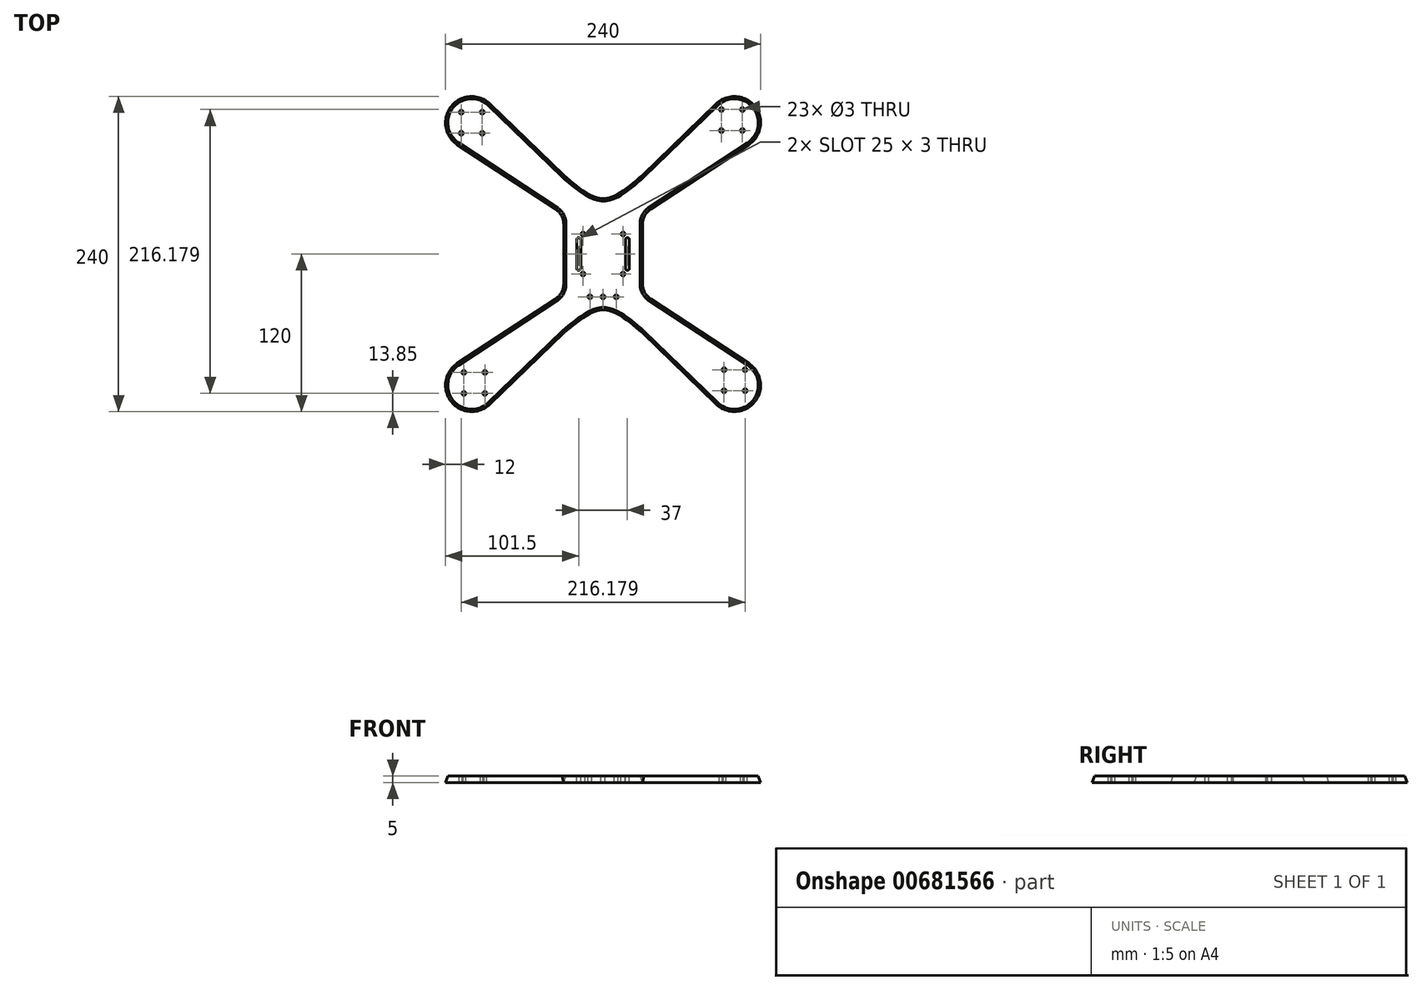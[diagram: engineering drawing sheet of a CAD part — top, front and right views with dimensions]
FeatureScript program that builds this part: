
annotation { "Feature Type Name" : "Feature", "Feature Type Description" : "" }
export const myFeature = defineFeature(function(context is Context, id is Id, definition is map)
    precondition{}
    {
        {
            var Q0;
            Q0=qCreatedBy(makeId("Top.planeOp"),FACE);
            var sketch = newSketch(context, id + "F0", { "sketchPlane" : qUnion([Q0])});
            skLineSegment(sketch, "E0.bottom", {"start": v(100, -100) * mm, "end": v(-100, -100) * mm, "construction": true});
            skLineSegment(sketch, "E0.top", {"start": v(100, 100) * mm, "end": v(-100, 100) * mm, "construction": true});
            skLineSegment(sketch, "E0.left", {"start": v(100, -100) * mm, "end": v(100, 100) * mm, "construction": true});
            skLineSegment(sketch, "E0.right", {"start": v(-100, -100) * mm, "end": v(-100, 100) * mm, "construction": true});
            skPoint(sketch, "E0.middle", {"position": v(0, 0) * mm});
            skLineSegment(sketch, "E1", {"start": v(0, 0) * mm, "end": v(-100, 100) * mm, "construction": true});
            skLineSegment(sketch, "E2", {"start": v(0, 0) * mm, "end": v(100, 100) * mm, "construction": true});
            skLineSegment(sketch, "E3", {"start": v(0, 0) * mm, "end": v(-100, -100) * mm, "construction": true});
            skLineSegment(sketch, "E4", {"start": v(0, 0) * mm, "end": v(100, -100) * mm, "construction": true});
            skCircle(sketch, "E5", {"center": v(-100, 100) * mm, "radius": 76.5 * mm, "construction": true});
            skCircle(sketch, "E6", {"center": v(100, 100) * mm, "radius": 76.5 * mm, "construction": true});
            skCircle(sketch, "E7", {"center": v(-100, -100) * mm, "radius": 76.5 * mm, "construction": true});
            skCircle(sketch, "E8", {"center": v(100, -100) * mm, "radius": 76.5 * mm, "construction": true});
            skSolve(sketch);
        }
        {
            var Q0;
            Q0=qCreatedBy(makeId("Top.planeOp"),FACE);
            var sketch = newSketch(context, id + "F1", { "sketchPlane" : qUnion([Q0])});
            skPoint(sketch, "E9.0", {"position": v(-100, 100) * mm});
            skPoint(sketch, "E10.0", {"position": v(100, 100) * mm});
            skPoint(sketch, "E11.0", {"position": v(100, -100) * mm});
            skPoint(sketch, "E12.0", {"position": v(-100, -100) * mm});
            skCircle(sketch, "E13", {"center": v(-100, 100) * mm, "radius": 20 * mm});
            skCircle(sketch, "E14", {"center": v(100, 100) * mm, "radius": 20 * mm});
            skCircle(sketch, "E15", {"center": v(-100, -100) * mm, "radius": 20 * mm});
            skCircle(sketch, "E16", {"center": v(100, -100) * mm, "radius": 20 * mm});
            skLineSegment(sketch, "E17.left", {"start": v(30, -60) * mm, "end": v(30, 60) * mm});
            skLineSegment(sketch, "E17.right", {"start": v(-30, -60) * mm, "end": v(-30, 60) * mm});
            skPoint(sketch, "E17.middle", {"position": v(0, 0) * mm});
            skLineSegment(sketch, "E18", {"start": v(30, 60) * mm, "end": v(86.08, 114.36) * mm});
            skLineSegment(sketch, "E19.0", {"start": v(0, 0) * mm, "end": v(-100, 100) * mm, "construction": true});
            skLineSegment(sketch, "E20.0", {"start": v(0, 0) * mm, "end": v(100, 100) * mm, "construction": true});
            skLineSegment(sketch, "E21.0", {"start": v(0, 0) * mm, "end": v(100, -100) * mm, "construction": true});
            skLineSegment(sketch, "E22.0", {"start": v(0, 0) * mm, "end": v(-100, -100) * mm, "construction": true});
            skLineSegment(sketch, "E23", {"start": v(30, 30) * mm, "end": v(111, 83.3) * mm});
            skLineSegment(sketch, "E24", {"start": v(-30, 60) * mm, "end": v(-86.08, 114.36) * mm});
            skLineSegment(sketch, "E25", {"start": v(-30, 30) * mm, "end": v(-111, 83.3) * mm});
            skLineSegment(sketch, "E26", {"start": v(30, -30) * mm, "end": v(111, -83.3) * mm});
            skLineSegment(sketch, "E27", {"start": v(30, -60) * mm, "end": v(86.08, -114.36) * mm});
            skLineSegment(sketch, "E28", {"start": v(-30, -30) * mm, "end": v(-111, -83.3) * mm});
            skLineSegment(sketch, "E29", {"start": v(-30, -60) * mm, "end": v(-86.08, -114.36) * mm});
            skFitSpline(sketch, "E30", {"points": [v(-30, -60) * mm, v(0, -42.43) * mm, v(30, -60) * mm], "startDerivative": vector(69.1, 55.46) * mm, "endDerivative": vector(68.94, -58.59) * mm});
            skFitSpline(sketch, "E31", {"points": [v(-30, 60) * mm, v(0, 42.17) * mm, v(30, 60) * mm], "startDerivative": vector(69.89, -59.66) * mm, "endDerivative": vector(69.64, 61.12) * mm});
            skSolve(sketch);
        }
        {
            var Q0;
            Q0=qSketchRegion(id+"F1",true);
            extrude(context, id + "F2", {"entities" : qUnion([Q0]), "depth" : 5 * mm, "offsetDistance" : 25 * mm, "hasDraft" : true, "draftAngle" : 20 * degree, "draftPullDirection" : true});
        }
        {
            var Q0;
            Q0=makeQuery(id+"F2.opExtrude","SWEPT_EDGE",EDGE,{"disambiguationData":[OSD([sQuery(id+"F1.wireOp",EDGE,"E17.right"),sQuery(id+"F1.wireOp",EDGE,"E25")])]});
            var Q1;
            Q1=makeQuery(id+"F2.opExtrude","SWEPT_EDGE",EDGE,{"disambiguationData":[OSD([sQuery(id+"F1.wireOp",EDGE,"E17.right"),sQuery(id+"F1.wireOp",EDGE,"E28")])]});
            var Q2;
            Q2=makeQuery(id+"F2.opExtrude","SWEPT_EDGE",EDGE,{"disambiguationData":[OSD([sQuery(id+"F1.wireOp",EDGE,"E17.left"),sQuery(id+"F1.wireOp",EDGE,"E26")])]});
            var Q3;
            Q3=makeQuery(id+"F2.opExtrude","SWEPT_EDGE",EDGE,{"disambiguationData":[OSD([sQuery(id+"F1.wireOp",EDGE,"E17.left"),sQuery(id+"F1.wireOp",EDGE,"E23")])]});
            fillet(context, id + "F3", {"entities" : qUnion([Q0, Q1, Q2, Q3]), "tangentPropagation" : true, "radius" : 15 * mm, "defaultsChanged" : true, "vertexSettings" : [], "allowEdgeOverflow" : false});
        }
        {
            var Q0;
            Q0=makeQuery(id+"F2.opExtrude","CAP_FACE",FACE,{"disambiguationData":[OSD([sQuery(id+"F1.wireOp",EDGE,"E13"),sQuery(id+"F1.wireOp",EDGE,"E14"),sQuery(id+"F1.wireOp",EDGE,"E15"),sQuery(id+"F1.wireOp",EDGE,"E16"),sQuery(id+"F1.wireOp",EDGE,"E17.left"),sQuery(id+"F1.wireOp",EDGE,"E17.right"),sQuery(id+"F1.wireOp",EDGE,"E18"),sQuery(id+"F1.wireOp",EDGE,"E23"),sQuery(id+"F1.wireOp",EDGE,"E24"),sQuery(id+"F1.wireOp",EDGE,"E25"),sQuery(id+"F1.wireOp",EDGE,"E26"),sQuery(id+"F1.wireOp",EDGE,"E27"),sQuery(id+"F1.wireOp",EDGE,"E28"),sQuery(id+"F1.wireOp",EDGE,"E29"),sQuery(id+"F1.wireOp",EDGE,"E30"),sQuery(id+"F1.wireOp",EDGE,"E31")])],"isStart":false});
            var sketch = newSketch(context, id + "F4", { "sketchPlane" : qUnion([Q0])});
            skCircle(sketch, "E32", {"center": v(-15.25, 15.25) * mm, "radius": 1.5 * mm});
            skCircle(sketch, "E33", {"center": v(15.25, 15.25) * mm, "radius": 1.5 * mm});
            skCircle(sketch, "E34", {"center": v(-15.25, -15.25) * mm, "radius": 1.5 * mm});
            skCircle(sketch, "E35", {"center": v(15.25, -15.25) * mm, "radius": 1.5 * mm});
            skLineSegment(sketch, "E36.bottom", {"start": v(-92, 108) * mm, "end": v(-108, 108) * mm, "construction": true});
            skLineSegment(sketch, "E36.top", {"start": v(-92, 92) * mm, "end": v(-108, 92) * mm, "construction": true});
            skLineSegment(sketch, "E36.left", {"start": v(-92, 108) * mm, "end": v(-92, 92) * mm, "construction": true});
            skLineSegment(sketch, "E36.right", {"start": v(-108, 108) * mm, "end": v(-108, 92) * mm, "construction": true});
            skPoint(sketch, "E36.middle", {"position": v(-100, 100) * mm});
            skCircle(sketch, "E37", {"center": v(-108, 108) * mm, "radius": 1.5 * mm});
            skCircle(sketch, "E38", {"center": v(-92, 108) * mm, "radius": 1.5 * mm});
            skCircle(sketch, "E39", {"center": v(-108, 92) * mm, "radius": 1.5 * mm});
            skCircle(sketch, "E40", {"center": v(-92, 92) * mm, "radius": 1.5 * mm});
            skCircle(sketch, "E41.1.0", {"center": v(-105.97, -90.15) * mm, "radius": 1.5 * mm});
            skCircle(sketch, "E41.1.1", {"center": v(-89.97, -90.15) * mm, "radius": 1.5 * mm});
            skCircle(sketch, "E41.1.2", {"center": v(-89.97, -106.15) * mm, "radius": 1.5 * mm});
            skCircle(sketch, "E41.1.3", {"center": v(-105.97, -106.15) * mm, "radius": 1.5 * mm});
            skCircle(sketch, "E41.2.0", {"center": v(92.18, -104.12) * mm, "radius": 1.5 * mm});
            skCircle(sketch, "E41.2.1", {"center": v(92.18, -88.12) * mm, "radius": 1.5 * mm});
            skCircle(sketch, "E41.2.2", {"center": v(108.18, -88.12) * mm, "radius": 1.5 * mm});
            skCircle(sketch, "E41.2.3", {"center": v(108.18, -104.12) * mm, "radius": 1.5 * mm});
            skCircle(sketch, "E41.3.0", {"center": v(106.15, 94.03) * mm, "radius": 1.5 * mm});
            skCircle(sketch, "E41.3.1", {"center": v(90.15, 94.03) * mm, "radius": 1.5 * mm});
            skCircle(sketch, "E41.3.2", {"center": v(90.15, 110.03) * mm, "radius": 1.5 * mm});
            skCircle(sketch, "E41.3.3", {"center": v(106.15, 110.03) * mm, "radius": 1.5 * mm});
            skPoint(sketch, "E41.center", {"position": v(0.09, 1.94) * mm});
            skLineSegment(sketch, "E42.bottom", {"start": v(-15.25, 15.25) * mm, "end": v(15.25, 15.25) * mm, "construction": true});
            skLineSegment(sketch, "E42.top", {"start": v(-15.25, -15.25) * mm, "end": v(15.25, -15.25) * mm, "construction": true});
            skLineSegment(sketch, "E42.left", {"start": v(-15.25, 15.25) * mm, "end": v(-15.25, -15.25) * mm, "construction": true});
            skLineSegment(sketch, "E42.right", {"start": v(15.25, 15.25) * mm, "end": v(15.25, -15.25) * mm, "construction": true});
            skLineSegment(sketch, "E43", {"start": v(15.25, 15.25) * mm, "end": v(-15.25, -15.25) * mm});
            skLineSegment(sketch, "E44", {"start": v(-15.25, 15.25) * mm, "end": v(15.25, -15.25) * mm});
            skPoint(sketch, "E45", {"position": v(0, 0) * mm});
            skLineSegment(sketch, "E46", {"start": v(0, 15.25) * mm, "end": v(0, -15.25) * mm, "construction": true});
            skLineSegment(sketch, "E47", {"start": v(-18.5, 11) * mm, "end": v(-18.5, -11) * mm});
            skLineSegment(sketch, "E48", {"start": v(18.5, 11) * mm, "end": v(18.5, -11) * mm});
            skPoint(sketch, "E49", {"position": v(-18.5, 0) * mm});
            skArc(sketch, "E50.0.startCap", {"start": v(-20, 11) * mm, "mid": v(-18.5, 12.5) * mm, "end": v(-17, 11) * mm});
            skArc(sketch, "E50.0.endCap", {"start": v(-17, -11) * mm, "mid": v(-18.5, -12.5) * mm, "end": v(-20, -11) * mm});
            skLineSegment(sketch, "E50.0.left", {"start": v(-17, 11) * mm, "end": v(-17, -11) * mm});
            skLineSegment(sketch, "E50.0.right", {"start": v(-20, 11) * mm, "end": v(-20, -11) * mm});
            skArc(sketch, "E50.1.startCap", {"start": v(17, 11) * mm, "mid": v(18.5, 12.5) * mm, "end": v(20, 11) * mm});
            skArc(sketch, "E50.1.endCap", {"start": v(20, -11) * mm, "mid": v(18.5, -12.5) * mm, "end": v(17, -11) * mm});
            skLineSegment(sketch, "E50.1.left", {"start": v(20, 11) * mm, "end": v(20, -11) * mm});
            skLineSegment(sketch, "E50.1.right", {"start": v(17, 11) * mm, "end": v(17, -11) * mm});
            skLineSegment(sketch, "E51", {"start": v(-10, -32.61) * mm, "end": v(10, -32.61) * mm, "construction": true});
            skPoint(sketch, "E52", {"position": v(0, -32.61) * mm});
            skCircle(sketch, "E53", {"center": v(-10, -32.61) * mm, "radius": 1.5 * mm});
            skCircle(sketch, "E54", {"center": v(10, -32.61) * mm, "radius": 1.5 * mm});
            skCircle(sketch, "E55", {"center": v(0, -32.61) * mm, "radius": 1.5 * mm});
            skSolve(sketch);
        }
        {
            var Q0;
            Q0=qSketchRegion(id+"F4",true);
            extrude(context, id + "F5", {"entities" : qUnion([Q0]), "operationType" : NewBodyOperationType.REMOVE, "endBound" : BoundingType.UP_TO_NEXT, "oppositeDirection" : true, "depth" : 25 * mm, "offsetDistance" : 25 * mm});
        }
        {
            var Q0;
            Q0=makeQuery(id+"F2.opExtrude","CAP_FACE",FACE,{"disambiguationData":[OSD([sQuery(id+"F1.wireOp",EDGE,"E13"),sQuery(id+"F1.wireOp",EDGE,"E14"),sQuery(id+"F1.wireOp",EDGE,"E15"),sQuery(id+"F1.wireOp",EDGE,"E16"),sQuery(id+"F1.wireOp",EDGE,"E17.left"),sQuery(id+"F1.wireOp",EDGE,"E17.right"),sQuery(id+"F1.wireOp",EDGE,"E18"),sQuery(id+"F1.wireOp",EDGE,"E23"),sQuery(id+"F1.wireOp",EDGE,"E24"),sQuery(id+"F1.wireOp",EDGE,"E25"),sQuery(id+"F1.wireOp",EDGE,"E26"),sQuery(id+"F1.wireOp",EDGE,"E27"),sQuery(id+"F1.wireOp",EDGE,"E28"),sQuery(id+"F1.wireOp",EDGE,"E29"),sQuery(id+"F1.wireOp",EDGE,"E30"),sQuery(id+"F1.wireOp",EDGE,"E31")])],"isStart":false});
            var sketch = newSketch(context, id + "F6", { "sketchPlane" : qUnion([Q0])});
            skSolve(sketch);
        }
    });
